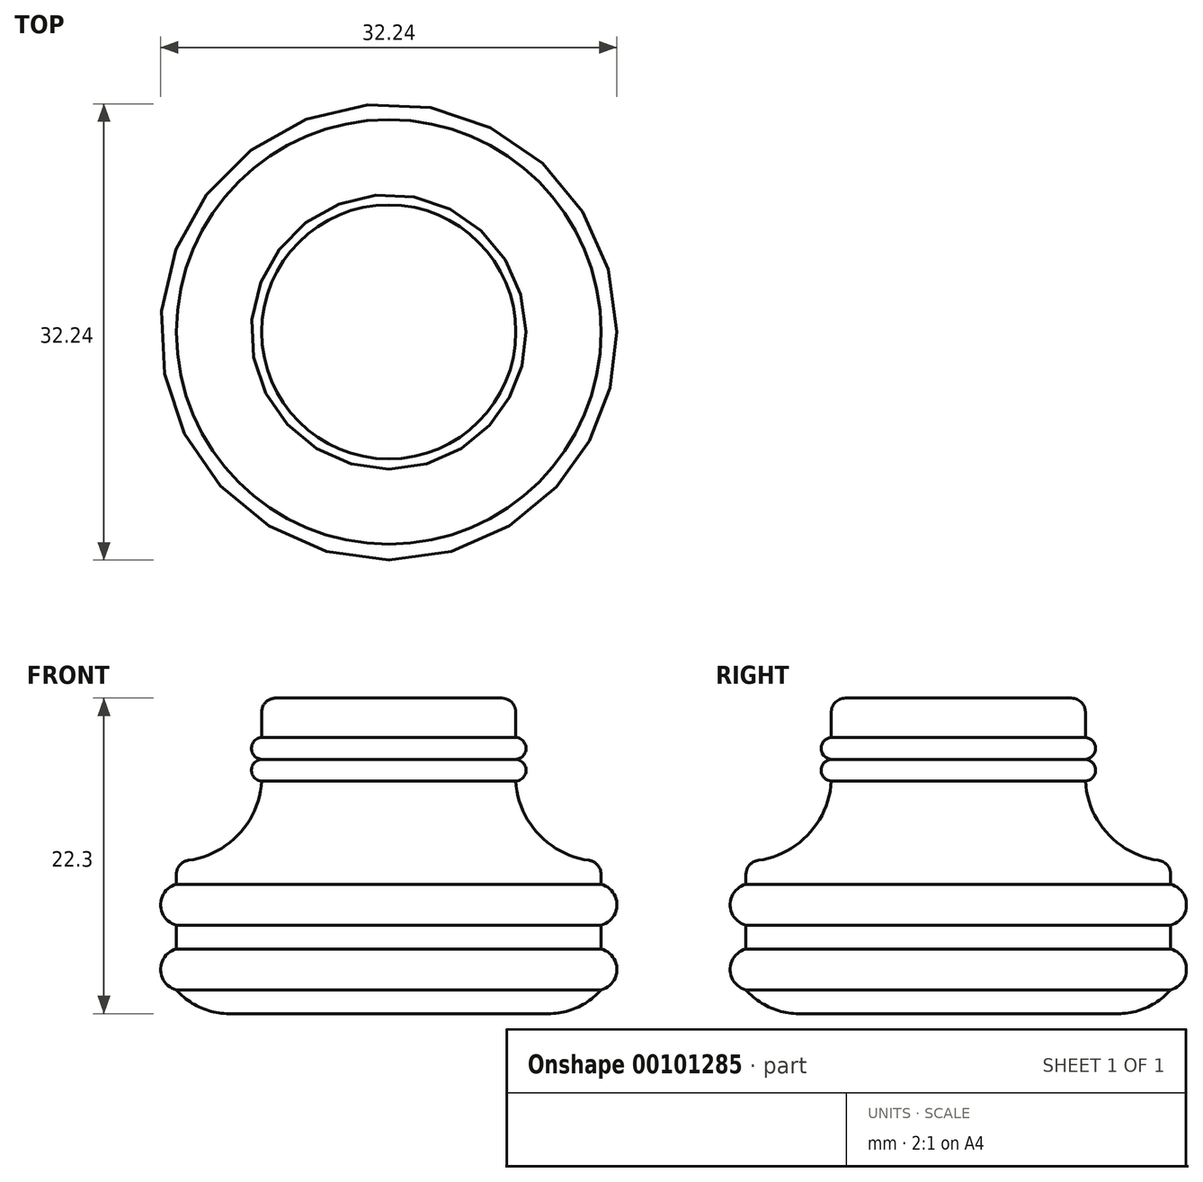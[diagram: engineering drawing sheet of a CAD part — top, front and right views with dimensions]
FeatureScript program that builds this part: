
annotation { "Feature Type Name" : "Feature", "Feature Type Description" : "" }
export const myFeature = defineFeature(function(context is Context, id is Id, definition is map)
    precondition{}
    {
        {
            var Q0;
            Q0=qCreatedBy(makeId("Front.planeOp"),FACE);
            var sketch = newSketch(context, id + "F0", { "sketchPlane" : qUnion([Q0])});
            skLineSegment(sketch, "E0", {"start": v(-63.84, 43.99) * mm, "end": v(-63.84, 21.69) * mm});
            skLineSegment(sketch, "E1", {"start": v(-63.84, 21.69) * mm, "end": v(-48.84, 21.69) * mm});
            skLineSegment(sketch, "E2", {"start": v(-48.84, 21.69) * mm, "end": v(-48.84, 23.36) * mm});
            skArc(sketch, "E3", {"start": v(-48.84, 23.36) * mm, "mid": v(-47.72, 24.8) * mm, "end": v(-48.84, 26.26) * mm});
            skLineSegment(sketch, "E4", {"start": v(-48.84, 26.26) * mm, "end": v(-48.84, 27.93) * mm});
            skArc(sketch, "E5", {"start": v(-48.84, 27.93) * mm, "mid": v(-47.72, 29.38) * mm, "end": v(-48.84, 30.83) * mm});
            skLineSegment(sketch, "E6", {"start": v(-48.84, 30.83) * mm, "end": v(-48.84, 32.53) * mm});
            skLineSegment(sketch, "E7", {"start": v(-48.84, 32.53) * mm, "end": v(-54.86, 32.53) * mm});
            skLineSegment(sketch, "E8", {"start": v(-54.86, 32.53) * mm, "end": v(-54.86, 38.12) * mm});
            skArc(sketch, "E9", {"start": v(-54.86, 38.12) * mm, "mid": v(-54.14, 38.9) * mm, "end": v(-54.86, 39.66) * mm});
            skArc(sketch, "E10", {"start": v(-54.86, 39.66) * mm, "mid": v(-54.14, 40.43) * mm, "end": v(-54.86, 41.2) * mm});
            skLineSegment(sketch, "E11", {"start": v(-54.86, 41.2) * mm, "end": v(-54.86, 43.99) * mm});
            skLineSegment(sketch, "E12", {"start": v(-54.86, 43.99) * mm, "end": v(-63.84, 43.99) * mm});
            skSolve(sketch);
        }
        {
            var Q0;
            Q0=makeQuery(id+"F0.imprint","IMPRINT",FACE,{"disambiguationData":[TD([[makeQuery(id+"F0.imprint","IMPRINT",EDGE,{"derivedFrom":sQuery(id+"F0.wireOp",EDGE,"E0")}),1.0]])]});
            var Q1;
            Q1=sQuery(id+"F0.wireOp",EDGE,"E0");
            revolve(context, id + "F1", {"entities" : qUnion([Q0]), "axis" : qUnion([Q1]), "revolveType" : RevolveType.FULL});
        }
        {
            var Q0;
            Q0=makeQuery(id+"F1.opRevolve","SWEPT_EDGE",EDGE,{"disambiguationData":[OSD([sQuery(id+"F0.wireOp",EDGE,"E1"),sQuery(id+"F0.wireOp",EDGE,"E2")])]});
            fillet(context, id + "F2", {"entities" : qUnion([Q0]), "radius" : 5 * mm, "tangentPropagation" : true, "allowEdgeOverflow" : false});
        }
        {
            var Q0;
            Q0=makeQuery(id+"F1.opRevolve","SWEPT_EDGE",EDGE,{"disambiguationData":[OSD([sQuery(id+"F0.wireOp",EDGE,"E6"),sQuery(id+"F0.wireOp",EDGE,"E7")])]});
            fillet(context, id + "F3", {"entities" : qUnion([Q0]), "radius" : 1 * mm, "tangentPropagation" : true, "allowEdgeOverflow" : false});
        }
        {
            var Q0;
            Q0=makeQuery(id+"F1.opRevolve","SWEPT_EDGE",EDGE,{"disambiguationData":[OSD([sQuery(id+"F0.wireOp",EDGE,"E7"),sQuery(id+"F0.wireOp",EDGE,"E8")])]});
            fillet(context, id + "F4", {"entities" : qUnion([Q0]), "radius" : 6 * mm, "tangentPropagation" : true, "allowEdgeOverflow" : false});
        }
        {
            var Q0;
            Q0=makeQuery(id+"F1.opRevolve","SWEPT_EDGE",EDGE,{"disambiguationData":[OSD([sQuery(id+"F0.wireOp",EDGE,"E11"),sQuery(id+"F0.wireOp",EDGE,"E12")])]});
            fillet(context, id + "F5", {"entities" : qUnion([Q0]), "radius" : 1 * mm, "tangentPropagation" : true, "allowEdgeOverflow" : false});
        }
    });
